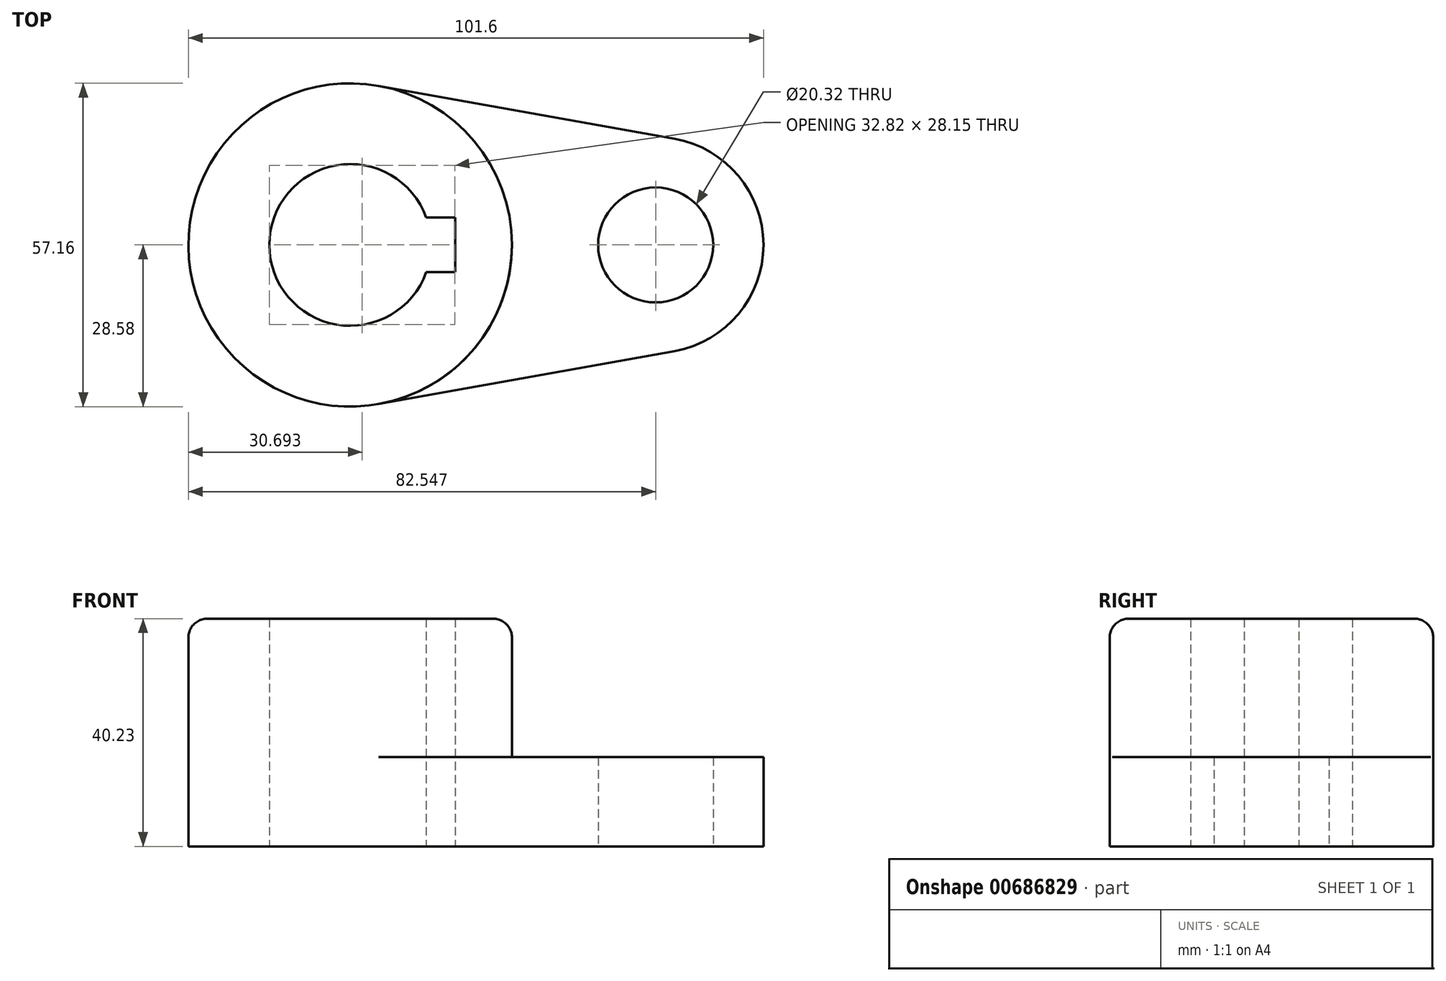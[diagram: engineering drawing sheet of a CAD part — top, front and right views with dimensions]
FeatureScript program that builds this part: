
annotation { "Feature Type Name" : "Feature", "Feature Type Description" : "" }
export const myFeature = defineFeature(function(context is Context, id is Id, definition is map)
    precondition{}
    {
        {
            var Q0;
            Q0=qCreatedBy(makeId("Top.planeOp"),FACE);
            var sketch = newSketch(context, id + "F0", { "sketchPlane" : qUnion([Q0])});
            skCircle(sketch, "E0", {"center": v(-26.99, 0) * mm, "radius": 14.29 * mm});
            skCircle(sketch, "E1", {"center": v(-26.99, 0) * mm, "radius": 28.58 * mm});
            skCircle(sketch, "E2", {"center": v(26.99, 0) * mm, "radius": 10.16 * mm});
            skCircle(sketch, "E3", {"center": v(26.99, 0) * mm, "radius": 19.05 * mm});
            skLineSegment(sketch, "E4", {"start": v(-21.94, 28.13) * mm, "end": v(30.35, 18.75) * mm});
            skLineSegment(sketch, "E5", {"start": v(-21.94, -28.13) * mm, "end": v(30.35, -18.75) * mm});
            skLineSegment(sketch, "E6", {"start": v(-8.46, 0) * mm, "end": v(-8.46, -4.83) * mm, "construction": true});
            skLineSegment(sketch, "E7", {"start": v(-8.46, -4.83) * mm, "end": v(-8.46, 4.83) * mm});
            skLineSegment(sketch, "E8", {"start": v(-8.46, 4.83) * mm, "end": v(-13.54, 4.83) * mm});
            skLineSegment(sketch, "E9", {"start": v(-8.46, -4.83) * mm, "end": v(-13.54, -4.83) * mm});
            skSolve(sketch);
        }
        {
            var Q0;
            {var subQ0=sQuery(id+"F0.wireOp",EDGE,"E4");Q0=makeQuery(id+"F0.imprint","IMPRINT",FACE,{"disambiguationData":[TD([[makeQuery(id+"F0.imprint","IMPRINT",EDGE,{"derivedFrom":subQ0}),-1.0]])]});}
            var Q1;
            Q1=makeQuery(id+"F0.imprint","IMPRINT",FACE,{"disambiguationData":[TD([[makeQuery(id+"F0.imprint","IMPRINT",EDGE,{"derivedFrom":sQuery(id+"F0.wireOp",EDGE,"E2")}),-1.0]])]});
            extrude(context, id + "F1", {"entities" : qUnion([Q0, Q1]), "depth" : 15.77 * mm, "offsetDistance" : 25.4 * mm});
        }
        {
            var Q0;
            Q0=makeQuery(id+"F0.imprint","IMPRINT",FACE,{"disambiguationData":[TD([[makeQuery(id+"F0.imprint","IMPRINT",EDGE,{"derivedFrom":sQuery(id+"F0.wireOp",EDGE,"E7")}),-1.0]])]});
            extrude(context, id + "F2", {"entities" : qUnion([Q0]), "operationType" : NewBodyOperationType.ADD, "depth" : 40.23 * mm, "offsetDistance" : 25.4 * mm});
        }
        {
            var Q0;
            Q0=makeQuery(id+"F2.opExtrude","CAP_EDGE",EDGE,{"disambiguationData":[OSD([sQuery(id+"F0.wireOp",EDGE,"E1")])],"isStart":false});
            fillet(context, id + "F3", {"entities" : qUnion([Q0]), "radius" : 3.3 * mm, "tangentPropagation" : true, "allowEdgeOverflow" : false});
        }
    });
